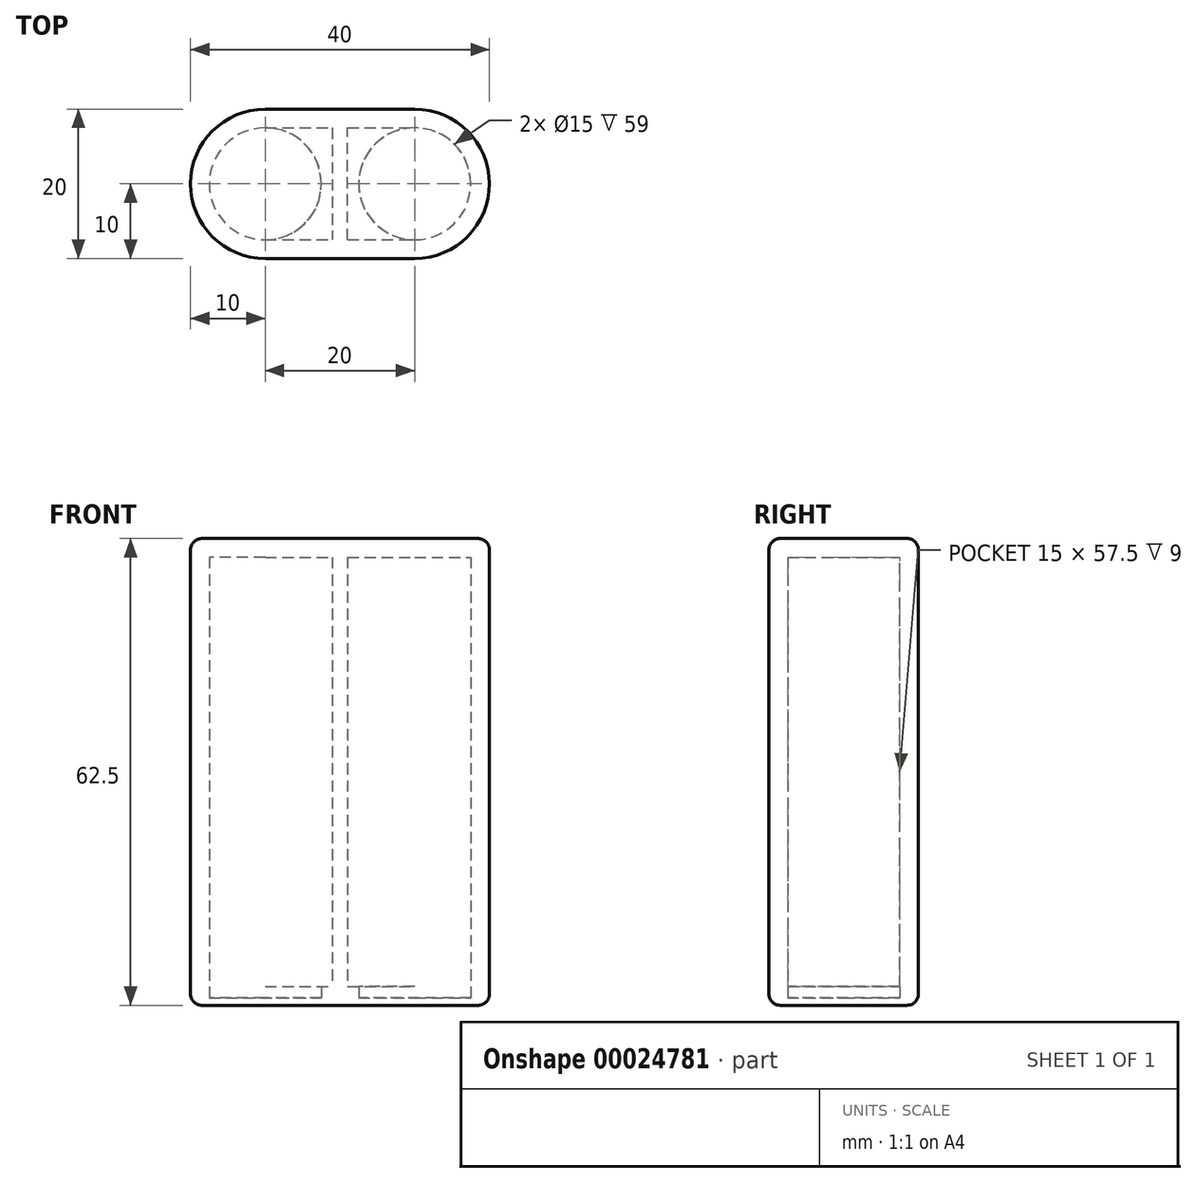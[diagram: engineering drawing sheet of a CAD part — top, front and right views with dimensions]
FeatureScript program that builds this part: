
annotation { "Feature Type Name" : "Feature", "Feature Type Description" : "" }
export const myFeature = defineFeature(function(context is Context, id is Id, definition is map)
    precondition{}
    {
        {
            var Q0;
            Q0=qCreatedBy(makeId("Top.planeOp"),FACE);
            var sketch = newSketch(context, id + "F0", { "sketchPlane" : qUnion([Q0])});
            skCircle(sketch, "E0", {"center": v(-10, 0) * mm, "radius": 10 * mm});
            skCircle(sketch, "E1", {"center": v(10, 0) * mm, "radius": 10 * mm});
            skLineSegment(sketch, "E2", {"start": v(-10, 0) * mm, "end": v(-10, -10) * mm});
            skLineSegment(sketch, "E3", {"start": v(-10, -10) * mm, "end": v(10, -10) * mm});
            skLineSegment(sketch, "E4", {"start": v(10, -10) * mm, "end": v(10, 0) * mm});
            skLineSegment(sketch, "E5", {"start": v(-10, 0) * mm, "end": v(-10, 10) * mm});
            skLineSegment(sketch, "E6", {"start": v(-10, 10) * mm, "end": v(10, 10) * mm});
            skLineSegment(sketch, "E7", {"start": v(10, 10) * mm, "end": v(10, 0) * mm});
            skSolve(sketch);
        }
        {
            var Q0;
            Q0 = qSketchRegion(id + "F0", true);
            extrude(context, id + "F1", {"entities" : qUnion([Q0]), "depth" : 60 * mm});
        }
        {
            var Q0;
            Q0=makeQuery(id+"F1.opExtrude","CAP_FACE",FACE,{"disambiguationData":[OSD([sQuery(id+"F0.wireOp",EDGE,"E0"),sQuery(id+"F0.wireOp",EDGE,"E1"),sQuery(id+"F0.wireOp",EDGE,"E3"),sQuery(id+"F0.wireOp",EDGE,"E6")])],"isStart":false});
            shell(context, id + "F2", {"entities" : qUnion([Q0]), "thickness" : 2.5 * mm});
        }
        {
            var Q0;
            Q0=makeQuery(id+"F2.opShell","OFFSET_FACE",FACE,{"disambiguationData":[OSD([sQuery(id+"F0.wireOp",EDGE,"E0"),sQuery(id+"F0.wireOp",EDGE,"E1"),sQuery(id+"F0.wireOp",EDGE,"E3"),sQuery(id+"F0.wireOp",EDGE,"E6")])]});
            var sketch = newSketch(context, id + "F3", { "sketchPlane" : qUnion([Q0])});
            skCircle(sketch, "E8", {"center": v(-10, 0) * mm, "radius": 7.5 * mm});
            skCircle(sketch, "E9", {"center": v(10, 0) * mm, "radius": 7.5 * mm});
            skSolve(sketch);
        }
        {
            var Q0;
            Q0 = qSketchRegion(id + "F3", true);
            extrude(context, id + "F4", {"entities" : qUnion([Q0]), "operationType" : NewBodyOperationType.REMOVE, "oppositeDirection" : true, "depth" : 1.5 * mm});
        }
        {
            var Q0;
            Q0=makeQuery(id+"F2.opShell","OFFSET_FACE",FACE,{"disambiguationData":[OSD([sQuery(id+"F0.wireOp",EDGE,"E0"),sQuery(id+"F0.wireOp",EDGE,"E1"),sQuery(id+"F0.wireOp",EDGE,"E3"),sQuery(id+"F0.wireOp",EDGE,"E6")])]});
            var sketch = newSketch(context, id + "F5", { "sketchPlane" : qUnion([Q0])});
            skLineSegment(sketch, "E10", {"start": v(-1, 7.5) * mm, "end": v(-1, -7.5) * mm});
            skLineSegment(sketch, "E11", {"start": v(-1, -7.5) * mm, "end": v(0, -7.5) * mm});
            skLineSegment(sketch, "E12", {"start": v(0, -7.5) * mm, "end": v(1, -7.5) * mm});
            skLineSegment(sketch, "E13", {"start": v(1, -7.5) * mm, "end": v(1, 7.5) * mm});
            skLineSegment(sketch, "E14", {"start": v(1, 7.5) * mm, "end": v(0, 7.5) * mm});
            skLineSegment(sketch, "E15", {"start": v(0, 7.5) * mm, "end": v(-1, 7.5) * mm});
            skSolve(sketch);
        }
        {
            var Q0;
            Q0 = qSketchRegion(id + "F5", true);
            extrude(context, id + "F6", {"entities" : qUnion([Q0]), "operationType" : NewBodyOperationType.ADD, "depth" : 57.5 * mm});
        }
        {
            var Q0;
            Q0=makeQuery(id+"F6.boolean.opBoolean","MERGE",FACE,{"derivedFrom":[makeQuery(id+"F1.opExtrude","CAP_FACE",FACE,{"disambiguationData":[OSD([sQuery(id+"F0.wireOp",EDGE,"E0"),sQuery(id+"F0.wireOp",EDGE,"E1"),sQuery(id+"F0.wireOp",EDGE,"E3"),sQuery(id+"F0.wireOp",EDGE,"E6")])],"isStart":false}),makeQuery(id+"F6.opExtrude","CAP_FACE",FACE,{"disambiguationData":[OSD([sQuery(id+"F5.wireOp",EDGE,"E10"),sQuery(id+"F5.wireOp",EDGE,"E11"),sQuery(id+"F5.wireOp",EDGE,"E12"),sQuery(id+"F5.wireOp",EDGE,"E13"),sQuery(id+"F5.wireOp",EDGE,"E14"),sQuery(id+"F5.wireOp",EDGE,"E15")])],"isStart":false})]});
            var sketch = newSketch(context, id + "F7", { "sketchPlane" : qUnion([Q0])});
            skLineSegment(sketch, "E16", {"start": v(10, -10) * mm, "end": v(10, 0) * mm});
            skCircle(sketch, "E17", {"center": v(10, 0) * mm, "radius": 10 * mm});
            skLineSegment(sketch, "E18", {"start": v(-10, 10) * mm, "end": v(10, 10) * mm});
            skLineSegment(sketch, "E19", {"start": v(-10, 0) * mm, "end": v(-10, 10) * mm});
            skLineSegment(sketch, "E20", {"start": v(-10, -10) * mm, "end": v(10, -10) * mm});
            skLineSegment(sketch, "E21", {"start": v(-10, 0) * mm, "end": v(-10, -10) * mm});
            skCircle(sketch, "E22", {"center": v(-10, 0) * mm, "radius": 10 * mm});
            skLineSegment(sketch, "E23", {"start": v(10, 10) * mm, "end": v(10, 0) * mm});
            skPoint(sketch, "E24", {"position": v(0, -10) * mm});
            skPoint(sketch, "E25", {"position": v(0, 10) * mm});
            skLineSegment(sketch, "E26", {"start": v(0, 10) * mm, "end": v(0, -10) * mm});
            skPoint(sketch, "E27", {"position": v(0, 0) * mm});
            skSolve(sketch);
        }
        {
            var Q0;
            Q0 = qSketchRegion(id + "F7", true);
            extrude(context, id + "F8", {"entities" : qUnion([Q0]), "operationType" : NewBodyOperationType.ADD, "depth" : 2.5 * mm});
        }
        {
            var Q0;
            Q0=makeQuery(id+"F8.opExtrude","CAP_EDGE",EDGE,{"disambiguationData":[OSD([sQuery(id+"F7.wireOp",EDGE,"E22")])],"isStart":false});
            var Q1;
            Q1=makeQuery(id+"F1.opExtrude","CAP_EDGE",EDGE,{"disambiguationData":[OSD([sQuery(id+"F0.wireOp",EDGE,"E0")])],"isStart":true});
            fillet(context, id + "F9", {"entities" : qUnion([Q0, Q1]), "radius" : 1.5 * mm, "tangentPropagation" : true, "allowEdgeOverflow" : false});
        }
    });
